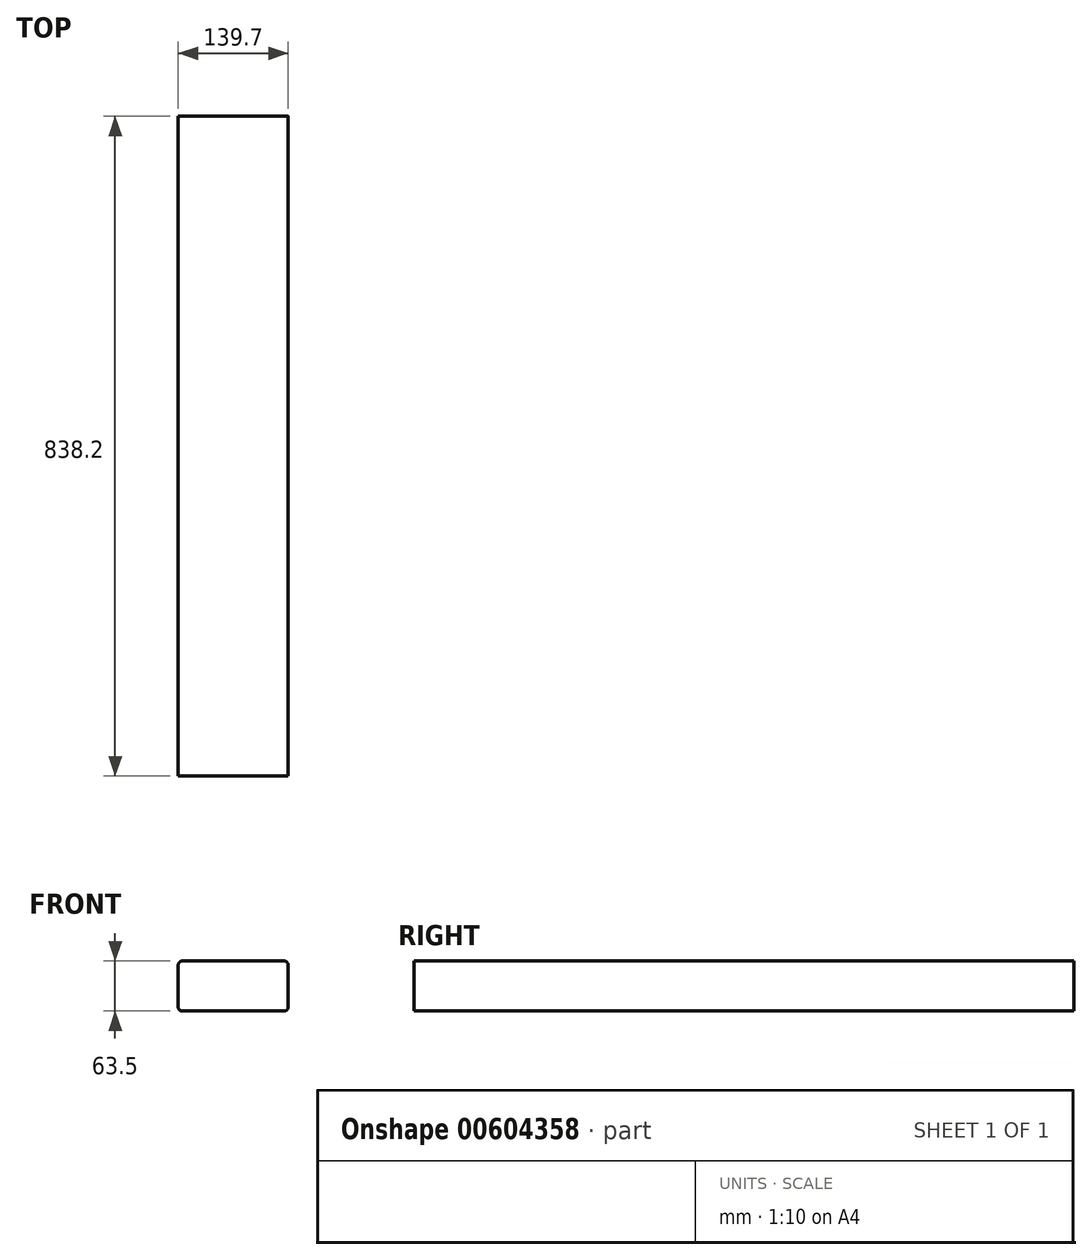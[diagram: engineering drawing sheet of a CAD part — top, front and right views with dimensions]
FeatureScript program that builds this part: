
annotation { "Feature Type Name" : "Feature", "Feature Type Description" : "" }
export const myFeature = defineFeature(function(context is Context, id is Id, definition is map)
    precondition{}
    {
        {
            var Q0;
            Q0=qCreatedBy(makeId("Front.planeOp"),FACE);
            var sketch = newSketch(context, id + "F0", { "sketchPlane" : qUnion([Q0])});
            skLineSegment(sketch, "E0.bottom", {"start": v(-69.85, 31.75) * mm, "end": v(69.85, 31.75) * mm});
            skLineSegment(sketch, "E0.top", {"start": v(-69.85, -31.75) * mm, "end": v(69.85, -31.75) * mm});
            skLineSegment(sketch, "E0.left", {"start": v(-69.85, 31.75) * mm, "end": v(-69.85, -31.75) * mm});
            skLineSegment(sketch, "E0.right", {"start": v(69.85, 31.75) * mm, "end": v(69.85, -31.75) * mm});
            skPoint(sketch, "E0.middle", {"position": v(0, 0) * mm});
            skSolve(sketch);
        }
        {
            var Q0;
            Q0=makeQuery(id+"F0.imprint","IMPRINT",FACE,{"disambiguationData":[TD([[makeQuery(id+"F0.imprint","IMPRINT",EDGE,{"derivedFrom":sQuery(id+"F0.wireOp",EDGE,"E0.bottom")}),-1.0]])]});
            extrude(context, id + "F1", {"entities" : qUnion([Q0]), "depth" : 838.2 * mm, "offsetDistance" : 25.4 * mm});
        }
        {
            var Q0;
            Q0=makeQuery(id+"F1.opExtrude","SWEPT_EDGE",EDGE,{"disambiguationData":[OSD([sQuery(id+"F0.wireOp",EDGE,"E0.bottom"),sQuery(id+"F0.wireOp",EDGE,"E0.right")])]});
            var Q1;
            Q1=makeQuery(id+"F1.opExtrude","SWEPT_EDGE",EDGE,{"disambiguationData":[OSD([sQuery(id+"F0.wireOp",EDGE,"E0.top"),sQuery(id+"F0.wireOp",EDGE,"E0.right")])]});
            var Q2;
            Q2=makeQuery(id+"F1.opExtrude","SWEPT_EDGE",EDGE,{"disambiguationData":[OSD([sQuery(id+"F0.wireOp",EDGE,"E0.bottom"),sQuery(id+"F0.wireOp",EDGE,"E0.left")])]});
            var Q3;
            Q3=makeQuery(id+"F1.opExtrude","SWEPT_EDGE",EDGE,{"disambiguationData":[OSD([sQuery(id+"F0.wireOp",EDGE,"E0.top"),sQuery(id+"F0.wireOp",EDGE,"E0.left")])]});
            fillet(context, id + "F2", {"entities" : qUnion([Q0, Q1, Q2, Q3]), "radius" : 5.08 * mm, "tangentPropagation" : true, "allowEdgeOverflow" : false});
        }
    });
